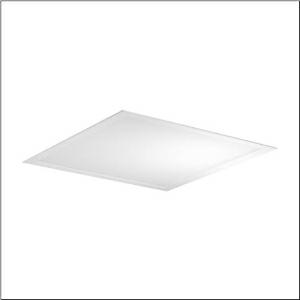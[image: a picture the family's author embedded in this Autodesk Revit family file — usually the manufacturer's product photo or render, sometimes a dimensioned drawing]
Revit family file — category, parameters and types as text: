
# Revit family: apollon_31_square_51mp11wd2n42
name_source: partatom
category: Lighting Fixtures
units: mm (PartAtom-declared; Revit-internal decimal feet)

## family parameters
Cut with Voids When Loaded = No
Host = Face
Light Source = No
Part Type = Normal
Room Calculation Point = No
Round Connector Dimension = Use Diameter
Shared = No

## types (1)
- --- (1 x LED, 4000 lm, 27.5 W, 5000K)
    Apparent Load = 28 VA
    CIE Flux Codes = 62 87 97 100 100
    Color Rendering = 80
    Color Temperature = 5000K
    Default Elevation = 1800 mm
    Description = Apollon 31 square, office luminaire, primary optical cover: micro prismatic cover, of PMMA, CAT 2 (L<= 3000cd/m²), light emission: direct distribution, primary light characteristic: symmetric, installation type: lay-in mounting, recessed, LED, rated luminous flux: 4.000lm, luminous efficacy: 145lm/W, light colour: 840/850, colour temperature: 4000/5000K, control gear: DALI 2, Multilumen, with terminal, 5-pole, mains connection: 220..240V, AC/DC, 0/50..60Hz, rated input power: 28W, suitable for self-contained emergency lighting element 58DB00B013A with integrated self-test function according to EN 60598-2-22, housing, of aluminium, coated, traffic white (RAL 9016), module: M625, length: 620mm, width: 620mm, height: 62mm, housing upper side, of sheet steel, coated, protection rating (complete): IP20, protection rating (lamp compartment, on room side): IP40, insulation class (complete): insulation class II (safety insulation), certification: CE, ENEC, impact resistance: IK03, permissible operating ambient temperature: -20..+40°C, standard: EN 60598-2-22, corresponds to IFS (International Featured Standards) requirements for safety and quality in the food industry, packaging unit: 1 piece
    Height = 0 mm  [stored 0 ft]
    Lamp = 1 x LED
    Lamp Light Flux = 4000 lm
    Lamp Power = 27.5 W
    Lamp count = 1
    Length = 620 mm
    Luminous efficacy = 145 lm/W
    Manufacturer = Siteco
    ModVariant = No
    Model = 51MP11WD2N42
    Mounting Place = Ceiling
    Mounting Type = Recessed
    Number of Poles = 1
    OnlyDefault = Yes
    Power Factor = 1
    Product Name = Apollon 31 square
    Product group = office luminaire | ceiling recessed
    ProductGroupID = 400
    Protection Class = Protection class II
    Protection Degree = IP 20
    RLX_Detail_Level = 1
    RLX_Emergency_Light_Flux = 0 lm
    RLX_Emergency_Type = 0
    RLX_Emergency_Type_DB = No
    RlxData = <blob elided: 13537 chars, md5=9a9ae30c>
    Socket = socket
    Standby Power = 0 W
    System Light Flux = 4000 lm
    System Power = 28 W
    Type Comments = individual setting: colour temperature 5000K
    Type Image = l_1291039.jpg
    URL = http://relux.com
    VarID = @adj_084365
    Voltage = 0 V
    Weight = 0.00 kg
    Width = 620 mm

note: [stored X ft] marks values corroborated as IEEE doubles in the binary element streams (Revit-internal decimal feet)

## geometry (parser evidence)
native form markers: Sweep x13
no freeform markers — native parametric forms only
